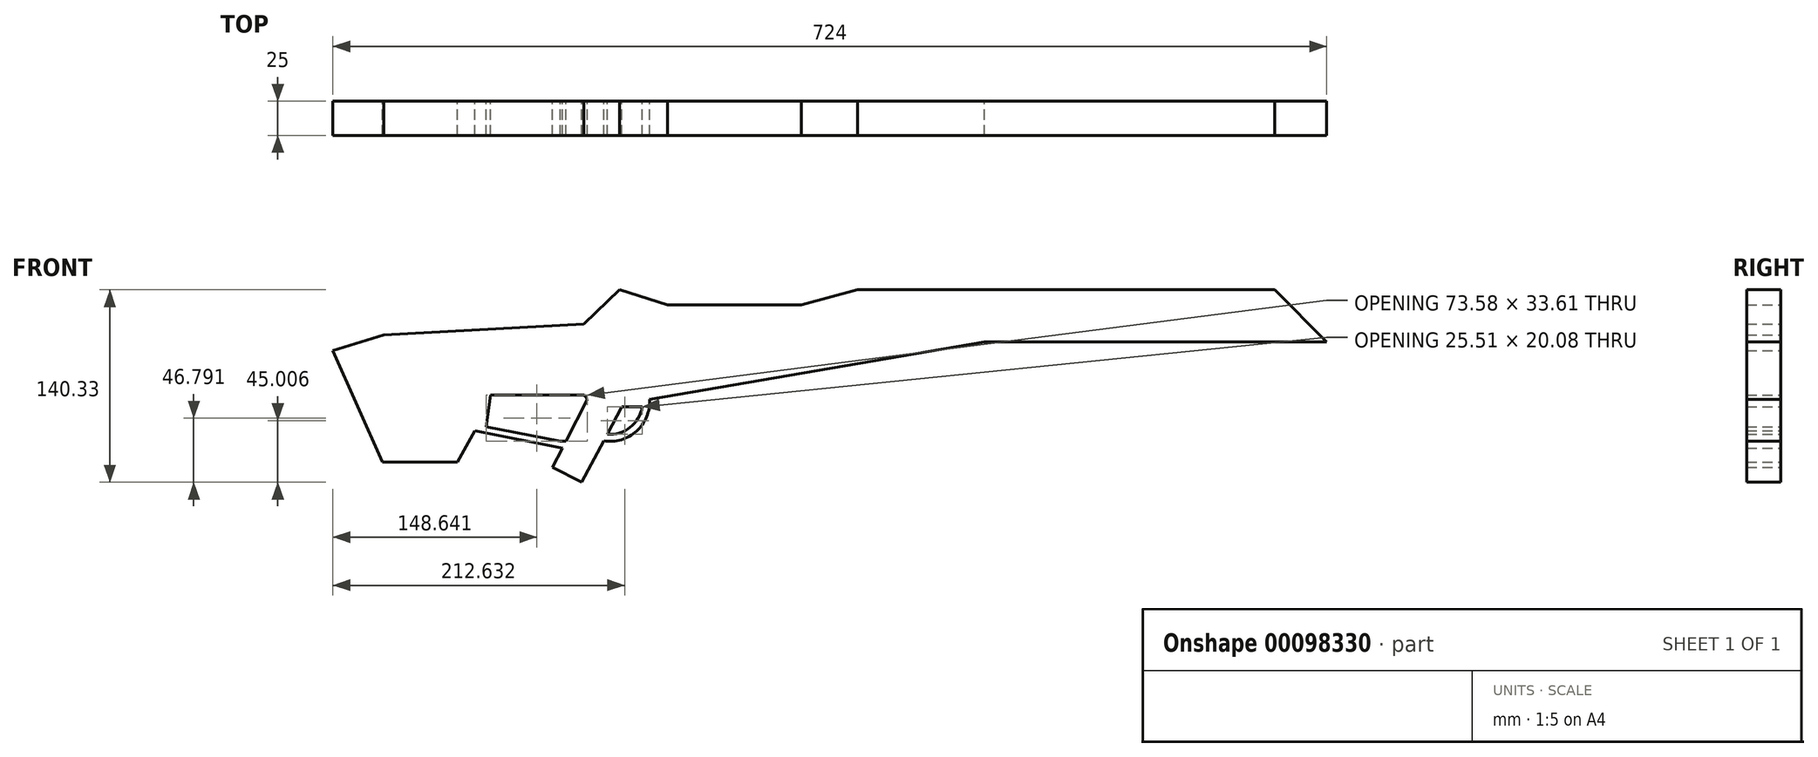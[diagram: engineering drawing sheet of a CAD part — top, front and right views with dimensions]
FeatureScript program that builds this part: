
annotation { "Feature Type Name" : "Feature", "Feature Type Description" : "" }
export const myFeature = defineFeature(function(context is Context, id is Id, definition is map)
    precondition{}
    {
        {
            var Q0;
            Q0=qCreatedBy(makeId("Front.planeOp"),FACE);
            var sketch = newSketch(context, id + "F0", { "sketchPlane" : qUnion([Q0])});
            skLineSegment(sketch, "E0.bottom", {"start": v(63.62, 37.88) * mm, "end": v(367.47, 37.88) * mm});
            skLineSegment(sketch, "E0.top", {"start": v(-133.22, -42.12) * mm, "end": v(-87.94, -42.12) * mm});
            skLineSegment(sketch, "E1", {"start": v(-109.66, -42.12) * mm, "end": v(-140.74, -100.7) * mm});
            skArc(sketch, "E2", {"start": v(-125.2, -71.4) * mm, "mid": v(-98.97, -66.43) * mm, "end": v(-87.94, -42.12) * mm});
            skLineSegment(sketch, "E3", {"start": v(-109.66, 37.88) * mm, "end": v(-135.77, 12.94) * mm});
            skLineSegment(sketch, "E4", {"start": v(-135.77, 12.94) * mm, "end": v(-281.5, 5.05) * mm});
            skLineSegment(sketch, "E5", {"start": v(-87.94, -42.12) * mm, "end": v(156.1, 0) * mm});
            skLineSegment(sketch, "E6", {"start": v(156.1, 0) * mm, "end": v(405.35, 0) * mm});
            skLineSegment(sketch, "E7", {"start": v(405.35, 0) * mm, "end": v(367.47, 37.88) * mm});
            skPoint(sketch, "E8.end.orphan", {"position": v(405.35, 37.88) * mm});
            skLineSegment(sketch, "E9", {"start": v(-140.74, -100.7) * mm, "end": v(-158.6, -91.52) * mm});
            skLineSegment(sketch, "E10", {"start": v(-281.5, 5.05) * mm, "end": v(-318.65, -6.35) * mm});
            skLineSegment(sketch, "E11", {"start": v(-318.65, -6.35) * mm, "end": v(-282.6, -87.82) * mm});
            skLineSegment(sketch, "E12", {"start": v(-282.6, -87.82) * mm, "end": v(-227.83, -87.82) * mm});
            skLineSegment(sketch, "E13", {"start": v(-227.83, -87.82) * mm, "end": v(-215.27, -64.97) * mm});
            skLineSegment(sketch, "E14", {"start": v(-215.27, -64.97) * mm, "end": v(-158.87, -75.99) * mm});
            skArc(sketch, "E15", {"start": v(-122.77, -66.82) * mm, "mid": v(-101.6, -62.04) * mm, "end": v(-93.02, -42.12) * mm});
            skLineSegment(sketch, "E16", {"start": v(-118.77, -67.48) * mm, "end": v(-108.12, -47.4) * mm});
            skLineSegment(sketch, "E17", {"start": v(-108.12, -47.4) * mm, "end": v(-93.26, -47.4) * mm});
            skLineSegment(sketch, "E18", {"start": v(-211.99, -42.12) * mm, "end": v(-215.27, -64.97) * mm});
            skLineSegment(sketch, "E19", {"start": v(-109.66, 37.88) * mm, "end": v(-74.7, 26.79) * mm});
            skLineSegment(sketch, "E20", {"start": v(-74.7, 26.79) * mm, "end": v(22.53, 26.79) * mm});
            skLineSegment(sketch, "E21", {"start": v(22.53, 26.79) * mm, "end": v(63.62, 37.88) * mm});
            skLineSegment(sketch, "E22", {"start": v(-206.8, -61.94) * mm, "end": v(-161.94, -70.7) * mm});
            skLineSegment(sketch, "E23", {"start": v(-211.99, -42.12) * mm, "end": v(-210.62, -32.64) * mm});
            skLineSegment(sketch, "E24", {"start": v(-210.62, -32.64) * mm, "end": v(-136.6, -32.64) * mm});
            skLineSegment(sketch, "E25", {"start": v(-203.63, -38.85) * mm, "end": v(-145.58, -38.85) * mm});
            skLineSegment(sketch, "E26", {"start": v(-203.63, -38.85) * mm, "end": v(-206.8, -61.94) * mm});
            skLineSegment(sketch, "E27", {"start": v(-136.6, -32.64) * mm, "end": v(-128.11, -32.18) * mm});
            skLineSegment(sketch, "E28", {"start": v(-128.11, -32.18) * mm, "end": v(-158.6, -91.52) * mm});
            skLineSegment(sketch, "E29", {"start": v(-158.87, -75.99) * mm, "end": v(-151.38, -77.45) * mm});
            skLineSegment(sketch, "E30", {"start": v(-145.58, -38.85) * mm, "end": v(-135.61, -38.85) * mm});
            skLineSegment(sketch, "E31", {"start": v(-161.94, -70.7) * mm, "end": v(-152.89, -72.46) * mm});
            skPoint(sketch, "E32.orphan", {"position": v(-154.7, -75.99) * mm});
            skLineSegment(sketch, "E33", {"start": v(-135.61, -38.85) * mm, "end": v(-133.22, -42.12) * mm});
            skLineSegment(sketch, "E34", {"start": v(-152.89, -72.46) * mm, "end": v(-148.81, -72.46) * mm});
            skLineSegment(sketch, "E35", {"start": v(-140.74, -100.7) * mm, "end": v(-137.32, -102.45) * mm});
            skLineSegment(sketch, "E36", {"start": v(-121.32, -72.29) * mm, "end": v(-137.32, -102.45) * mm});
            skPoint(sketch, "E37.orphan", {"position": v(-118.77, -111.99) * mm});
            skSolve(sketch);
        }
        {
            var Q0;
            Q0=makeQuery(id+"F0.imprint","IMPRINT",FACE,{"disambiguationData":[TD([[makeQuery(id+"F0.imprint","IMPRINT",EDGE,{"derivedFrom":sQuery(id+"F0.wireOp",EDGE,"E0.bottom")}),-1.0]])]});
            var Q1;
            {var subQ0=sQuery(id+"F0.wireOp",EDGE,"E9");Q1=makeQuery(id+"F0.imprint","IMPRINT",FACE,{"disambiguationData":[TD([[makeQuery(id+"F0.imprint","IMPRINT",EDGE,{"derivedFrom":subQ0}),-1.0]])]});}
            var Q2;
            {var subQ4=sQuery(id+"F0.wireOp",EDGE,"E2");Q2=makeQuery(id+"F0.imprint","IMPRINT",FACE,{"disambiguationData":[TD([[makeQuery(id+"F0.imprint","IMPRINT",EDGE,{"derivedFrom":subQ4}),1.0]])]});}
            var Q3;
            {var subQ3=sQuery(id+"F0.wireOp",EDGE,"E16");Q3=makeQuery(id+"F0.imprint","IMPRINT",FACE,{"disambiguationData":[TD([[makeQuery(id+"F0.imprint","IMPRINT",EDGE,{"derivedFrom":subQ3}),1.0]])]});}
            var Q4;
            {var subQ1=sQuery(id+"F0.wireOp",EDGE,"E14");Q4=makeQuery(id+"F0.imprint","IMPRINT",FACE,{"disambiguationData":[TD([[makeQuery(id+"F0.imprint","IMPRINT",EDGE,{"derivedFrom":subQ1}),1.0]])]});}
            var Q5;
            {var subQ0=sQuery(id+"F0.wireOp",EDGE,"E35");Q5=makeQuery(id+"F0.imprint","IMPRINT",FACE,{"disambiguationData":[TD([[makeQuery(id+"F0.imprint","IMPRINT",EDGE,{"derivedFrom":subQ0}),1.0]])]});}
            extrude(context, id + "F1", {"entities" : qUnion([Q0, Q1, Q2, Q3, Q4, Q5]), "depth" : 25 * mm});
        }
    });
